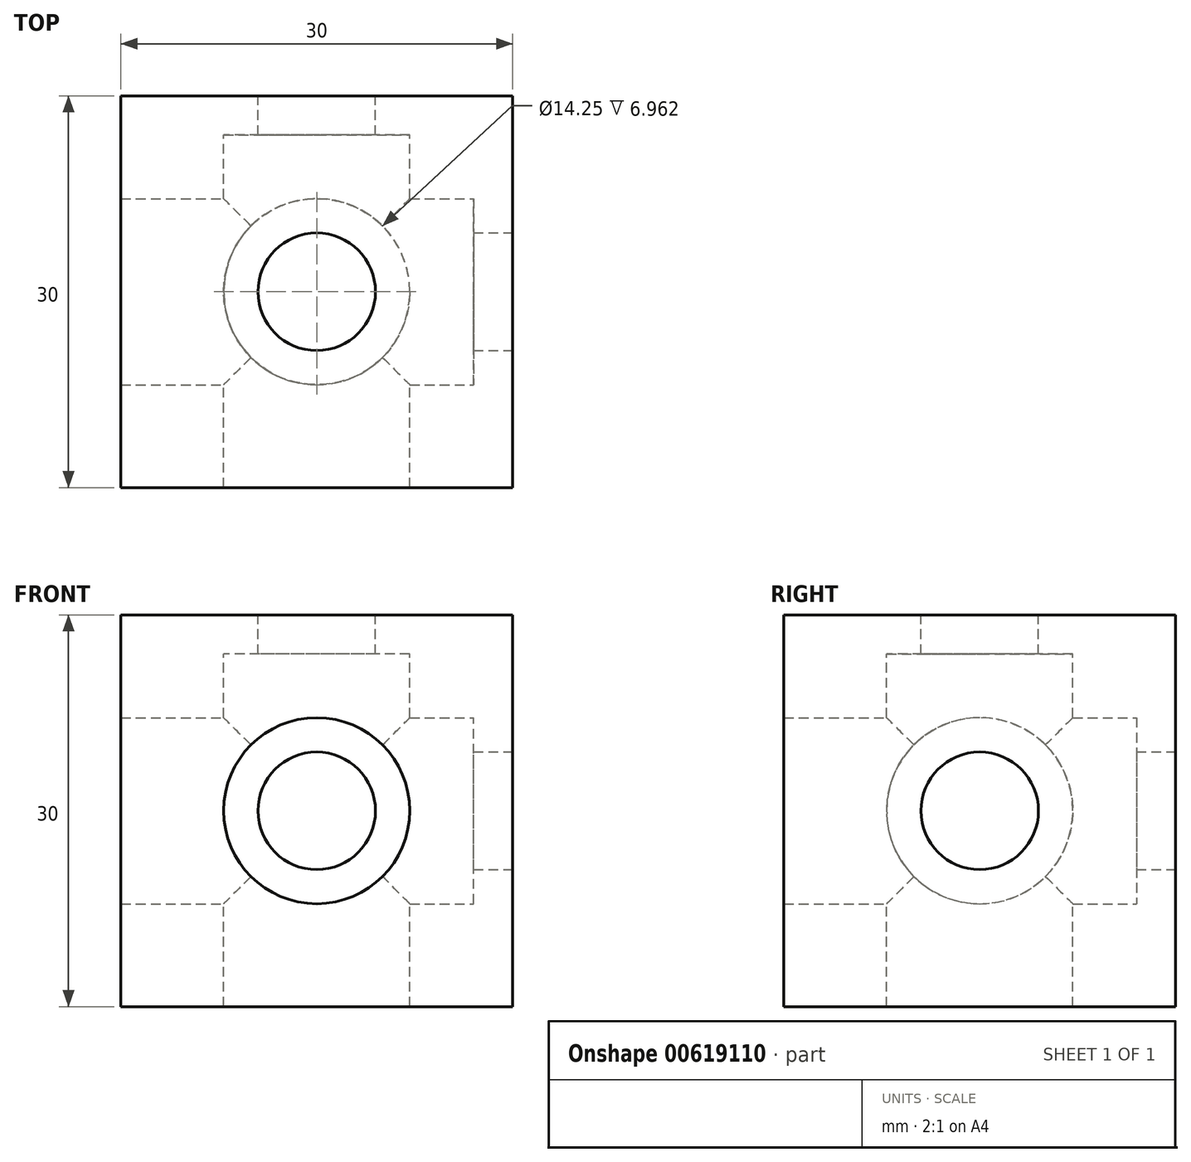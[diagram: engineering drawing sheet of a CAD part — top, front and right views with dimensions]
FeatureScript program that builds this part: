
annotation { "Feature Type Name" : "Feature", "Feature Type Description" : "" }
export const myFeature = defineFeature(function(context is Context, id is Id, definition is map)
    precondition{}
    {
        {
            var Q0;
            Q0=qCreatedBy(makeId("Front.planeOp"),FACE);
            var sketch = newSketch(context, id + "F0", { "sketchPlane" : qUnion([Q0])});
            skLineSegment(sketch, "E0.bottom", {"start": v(-15, 15) * mm, "end": v(15, 15) * mm});
            skLineSegment(sketch, "E0.top", {"start": v(-15, -15) * mm, "end": v(15, -15) * mm});
            skLineSegment(sketch, "E0.left", {"start": v(-15, 15) * mm, "end": v(-15, -15) * mm});
            skLineSegment(sketch, "E0.right", {"start": v(15, 15) * mm, "end": v(15, -15) * mm});
            skPoint(sketch, "E0.middle", {"position": v(0, 0) * mm});
            skSolve(sketch);
        }
        {
            var Q0;
            Q0 = qSketchRegion(id + "F0", true);
            extrude(context, id + "F1", {"entities" : qUnion([Q0]), "depth" : 30 * mm, "offsetDistance" : 25 * mm});
        }
        {
            var Q0;
            Q0=makeQuery(id+"F1.opExtrude","CAP_FACE",FACE,{"disambiguationData":[OSD([sQuery(id+"F0.wireOp",EDGE,"E0.bottom"),sQuery(id+"F0.wireOp",EDGE,"E0.top"),sQuery(id+"F0.wireOp",EDGE,"E0.left"),sQuery(id+"F0.wireOp",EDGE,"E0.right")])],"isStart":false});
            var sketch = newSketch(context, id + "F2", { "sketchPlane" : qUnion([Q0])});
            skPoint(sketch, "E1", {"position": v(0, 0) * mm});
            skSolve(sketch);
        }
        {
            var Q0;
            Q0=sQuery(id+"F2.wireOp",VERTEX,"E1");
            var Q1;
            Q1=makeQuery(id+"F1.opExtrude","SWEPT_BODY",BODY,{"disambiguationData":[OSD([sQuery(id+"F0.wireOp",EDGE,"E0.bottom"),sQuery(id+"F0.wireOp",EDGE,"E0.top"),sQuery(id+"F0.wireOp",EDGE,"E0.left"),sQuery(id+"F0.wireOp",EDGE,"E0.right")])]});
            hole(context, id + "F3", {"style" : HoleStyle.C_BORE, "endStyle" : HoleEndStyle.THROUGH, "holeDiameter" : 9 * mm, "cBoreDiameter" : 14.25 * mm, "cBoreDepth" : 27 * mm, "majorDiameter" : 5 * mm, "isTappedThrough" : true, "tappedDepth" : 12 * mm, "tapClearance" : 3, "locations" : qUnion([Q0]), "scope" : qUnion([Q1]), "startStyle" : HoleStartStyle.SKETCH});
        }
        {
            var Q0;
            Q0=makeQuery(id+"F1.opExtrude","SWEPT_FACE",FACE,{"disambiguationData":[OSD([sQuery(id+"F0.wireOp",EDGE,"E0.left")])]});
            var sketch = newSketch(context, id + "F4", { "sketchPlane" : qUnion([Q0])});
            skPoint(sketch, "E2", {"position": v(15, 0) * mm});
            skPoint(sketch, "E2.positionSnap0", {"position": v(15, 15) * mm});
            skPoint(sketch, "E2.positionSnap1", {"position": v(0, 0) * mm});
            skSolve(sketch);
        }
        {
            var Q0;
            Q0=sQuery(id+"F4.wireOp",VERTEX,"E2");
            var Q1;
            Q1=makeQuery(id+"F1.opExtrude","SWEPT_BODY",BODY,{"disambiguationData":[OSD([sQuery(id+"F0.wireOp",EDGE,"E0.bottom"),sQuery(id+"F0.wireOp",EDGE,"E0.top"),sQuery(id+"F0.wireOp",EDGE,"E0.left"),sQuery(id+"F0.wireOp",EDGE,"E0.right")])]});
            hole(context, id + "F5", {"style" : HoleStyle.C_BORE, "endStyle" : HoleEndStyle.THROUGH, "holeDiameter" : 9 * mm, "cBoreDiameter" : 14.25 * mm, "cBoreDepth" : 27 * mm, "majorDiameter" : 5 * mm, "isTappedThrough" : true, "tappedDepth" : 12 * mm, "tapClearance" : 3, "locations" : qUnion([Q0]), "scope" : qUnion([Q1]), "startStyle" : HoleStartStyle.SKETCH});
        }
        {
            var Q0;
            Q0=makeQuery(id+"F1.opExtrude","SWEPT_FACE",FACE,{"disambiguationData":[OSD([sQuery(id+"F0.wireOp",EDGE,"E0.top")])]});
            var sketch = newSketch(context, id + "F6", { "sketchPlane" : qUnion([Q0])});
            skPoint(sketch, "E3", {"position": v(0, 15) * mm});
            skPoint(sketch, "E3.positionSnap0", {"position": v(-15, 15) * mm});
            skPoint(sketch, "E3.positionSnap1", {"position": v(0, 30) * mm});
            skSolve(sketch);
        }
        {
            var Q0;
            Q0=sQuery(id+"F6.wireOp",VERTEX,"E3");
            var Q1;
            Q1=makeQuery(id+"F1.opExtrude","SWEPT_BODY",BODY,{"disambiguationData":[OSD([sQuery(id+"F0.wireOp",EDGE,"E0.bottom"),sQuery(id+"F0.wireOp",EDGE,"E0.top"),sQuery(id+"F0.wireOp",EDGE,"E0.left"),sQuery(id+"F0.wireOp",EDGE,"E0.right")])]});
            hole(context, id + "F7", {"style" : HoleStyle.C_BORE, "endStyle" : HoleEndStyle.THROUGH, "holeDiameter" : 9 * mm, "cBoreDiameter" : 14.25 * mm, "cBoreDepth" : 27 * mm, "majorDiameter" : 5 * mm, "isTappedThrough" : true, "tappedDepth" : 12 * mm, "tapClearance" : 3, "locations" : qUnion([Q0]), "scope" : qUnion([Q1]), "startStyle" : HoleStartStyle.SKETCH});
        }
    });
